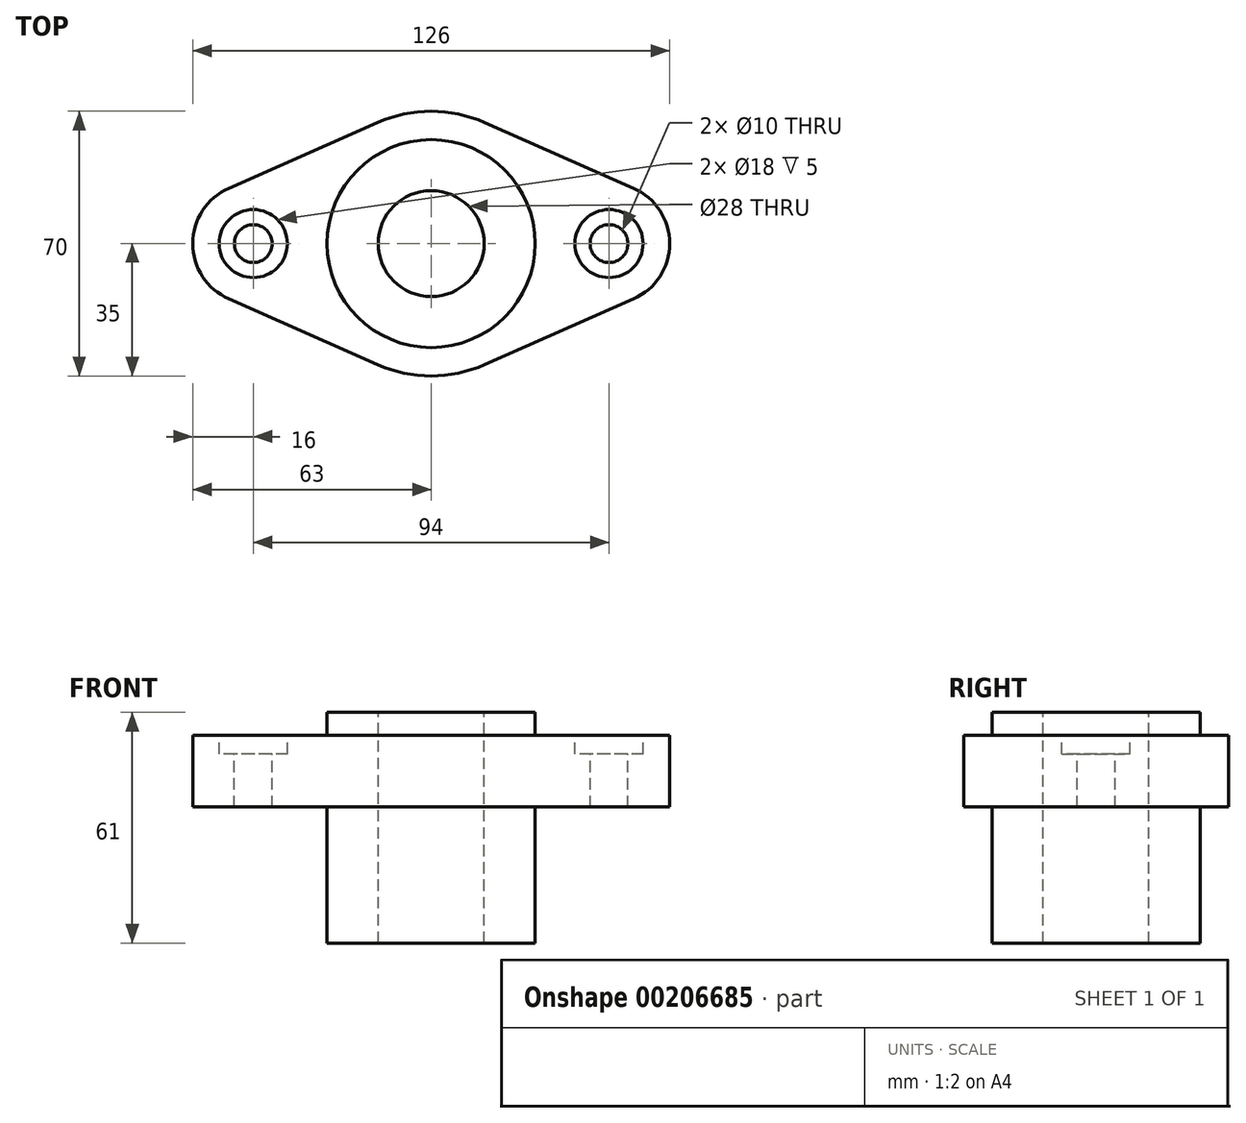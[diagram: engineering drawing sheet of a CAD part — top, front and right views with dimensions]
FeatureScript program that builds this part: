
annotation { "Feature Type Name" : "Feature", "Feature Type Description" : "" }
export const myFeature = defineFeature(function(context is Context, id is Id, definition is map)
    precondition{}
    {
        {
            var Q0;
            Q0=qCreatedBy(makeId("Top.planeOp"),FACE);
            var sketch = newSketch(context, id + "F0", { "sketchPlane" : qUnion([Q0])});
            skCircle(sketch, "E0", {"center": v(0, 0) * mm, "radius": 14 * mm});
            skCircle(sketch, "E1", {"center": v(0, 0) * mm, "radius": 27.5 * mm});
            skCircle(sketch, "E2", {"center": v(0, 0) * mm, "radius": 35 * mm});
            skCircle(sketch, "E3", {"center": v(-47, 0) * mm, "radius": 16 * mm});
            skCircle(sketch, "E4", {"center": v(47, 0) * mm, "radius": 16 * mm});
            skLineSegment(sketch, "E5", {"start": v(-53.47, 14.63) * mm, "end": v(-14.15, 32.01) * mm});
            skLineSegment(sketch, "E6", {"start": v(-53.47, -14.63) * mm, "end": v(-14.15, -32.01) * mm});
            skLineSegment(sketch, "E7", {"start": v(14.15, 32.01) * mm, "end": v(53.47, 14.63) * mm});
            skLineSegment(sketch, "E8", {"start": v(14.15, -32.01) * mm, "end": v(53.47, -14.63) * mm});
            skSolve(sketch);
        }
        {
            var Q0;
            {var subQ0=sQuery(id+"F0.wireOp",EDGE,"E3");var subQ1=sQuery(id+"F0.wireOp",EDGE,"E2");var subQ2=makeQuery(id+"F0.imprint","INTERSECT",VERTEX,{"disambiguationData":[OD(0.0)],"derivedFrom":[subQ1,subQ0]});Q0=makeQuery(id+"F0.imprint","IMPRINT",FACE,{"disambiguationData":[TD([[makeQuery(id+"F0.imprint","IMPRINT",EDGE,{"disambiguationData":[TD([[subQ2,-1.0]])],"derivedFrom":subQ1}),-1.0]])]});}
            var Q1;
            {var subQ0=sQuery(id+"F0.wireOp",EDGE,"E5");Q1=makeQuery(id+"F0.imprint","IMPRINT",FACE,{"disambiguationData":[TD([[makeQuery(id+"F0.imprint","IMPRINT",EDGE,{"derivedFrom":subQ0}),-1.0]])]});}
            var Q2;
            {var subQ0=sQuery(id+"F0.wireOp",EDGE,"E3");var subQ1=sQuery(id+"F0.wireOp",EDGE,"E2");var subQ2=makeQuery(id+"F0.imprint","INTERSECT",VERTEX,{"disambiguationData":[OD(0.0)],"derivedFrom":[subQ1,subQ0]});Q2=makeQuery(id+"F0.imprint","IMPRINT",FACE,{"disambiguationData":[TD([[makeQuery(id+"F0.imprint","IMPRINT",EDGE,{"disambiguationData":[TD([[subQ2,-1.0]])],"derivedFrom":subQ1}),1.0]])]});}
            var Q3;
            Q3=makeQuery(id+"F0.imprint","IMPRINT",FACE,{"disambiguationData":[TD([[makeQuery(id+"F0.imprint","IMPRINT",EDGE,{"derivedFrom":sQuery(id+"F0.wireOp",EDGE,"E1")}),-1.0]])]});
            var Q4;
            {var subQ0=sQuery(id+"F0.wireOp",EDGE,"E6");Q4=makeQuery(id+"F0.imprint","IMPRINT",FACE,{"disambiguationData":[TD([[makeQuery(id+"F0.imprint","IMPRINT",EDGE,{"derivedFrom":subQ0}),1.0]])]});}
            var Q5;
            Q5=makeQuery(id+"F0.imprint","IMPRINT",FACE,{"disambiguationData":[TD([[makeQuery(id+"F0.imprint","IMPRINT",EDGE,{"derivedFrom":sQuery(id+"F0.wireOp",EDGE,"E0")}),-1.0]])]});
            var Q6;
            {var subQ0=sQuery(id+"F0.wireOp",EDGE,"E4");var subQ1=sQuery(id+"F0.wireOp",EDGE,"E2");var subQ2=makeQuery(id+"F0.imprint","INTERSECT",VERTEX,{"disambiguationData":[OD(0.0)],"derivedFrom":[subQ1,subQ0]});Q6=makeQuery(id+"F0.imprint","IMPRINT",FACE,{"disambiguationData":[TD([[makeQuery(id+"F0.imprint","IMPRINT",EDGE,{"disambiguationData":[TD([[subQ2,1.0]])],"derivedFrom":subQ1}),-1.0]])]});}
            var Q7;
            {var subQ0=sQuery(id+"F0.wireOp",EDGE,"E4");var subQ1=sQuery(id+"F0.wireOp",EDGE,"E2");var subQ2=makeQuery(id+"F0.imprint","INTERSECT",VERTEX,{"disambiguationData":[OD(0.0)],"derivedFrom":[subQ1,subQ0]});Q7=makeQuery(id+"F0.imprint","IMPRINT",FACE,{"disambiguationData":[TD([[makeQuery(id+"F0.imprint","IMPRINT",EDGE,{"disambiguationData":[TD([[subQ2,1.0]])],"derivedFrom":subQ1}),1.0]])]});}
            var Q8;
            {var subQ0=sQuery(id+"F0.wireOp",EDGE,"E7");Q8=makeQuery(id+"F0.imprint","IMPRINT",FACE,{"disambiguationData":[TD([[makeQuery(id+"F0.imprint","IMPRINT",EDGE,{"derivedFrom":subQ0}),-1.0]])]});}
            var Q9;
            {var subQ0=sQuery(id+"F0.wireOp",EDGE,"E8");Q9=makeQuery(id+"F0.imprint","IMPRINT",FACE,{"disambiguationData":[TD([[makeQuery(id+"F0.imprint","IMPRINT",EDGE,{"derivedFrom":subQ0}),1.0]])]});}
            extrude(context, id + "F1", {"entities" : qUnion([Q0, Q1, Q2, Q3, Q4, Q5, Q6, Q7, Q8, Q9]), "oppositeDirection" : true, "depth" : 19 * mm});
        }
        {
            var Q0;
            Q0=makeQuery(id+"F0.imprint","IMPRINT",FACE,{"disambiguationData":[TD([[makeQuery(id+"F0.imprint","IMPRINT",EDGE,{"derivedFrom":sQuery(id+"F0.wireOp",EDGE,"E0")}),-1.0]])]});
            extrude(context, id + "F2", {"entities" : qUnion([Q0]), "operationType" : NewBodyOperationType.ADD, "depth" : 6 * mm});
        }
        {
            var Q0;
            Q0=makeQuery(id+"F1.opExtrude","CAP_FACE",FACE,{"disambiguationData":[OSD([sQuery(id+"F0.wireOp",EDGE,"E0"),sQuery(id+"F0.wireOp",EDGE,"E2"),sQuery(id+"F0.wireOp",EDGE,"E3"),sQuery(id+"F0.wireOp",EDGE,"E4"),sQuery(id+"F0.wireOp",EDGE,"E5"),sQuery(id+"F0.wireOp",EDGE,"E6"),sQuery(id+"F0.wireOp",EDGE,"E7"),sQuery(id+"F0.wireOp",EDGE,"E8")])],"isStart":false});
            var sketch = newSketch(context, id + "F3", { "sketchPlane" : qUnion([Q0])});
            skCircle(sketch, "E9", {"center": v(0, 0) * mm, "radius": 27.5 * mm});
            skCircle(sketch, "E10", {"center": v(0, 0) * mm, "radius": 14 * mm});
            skSolve(sketch);
        }
        {
            var Q0;
            Q0=makeQuery(id+"F3.imprint","IMPRINT",FACE,{"disambiguationData":[TD([[makeQuery(id+"F3.imprint","IMPRINT",EDGE,{"derivedFrom":sQuery(id+"F3.wireOp",EDGE,"E9")}),1.0]])]});
            extrude(context, id + "F4", {"entities" : qUnion([Q0]), "operationType" : NewBodyOperationType.ADD, "depth" : 36 * mm});
        }
        {
            var Q0;
            {var subQ0=sQuery(id+"F0.wireOp",EDGE,"E3");var subQ1=sQuery(id+"F0.wireOp",EDGE,"E2");var subQ2=makeQuery(id+"F0.imprint","INTERSECT",VERTEX,{"disambiguationData":[OD(0.0)],"derivedFrom":[subQ1,subQ0]});Q0=makeQuery(id+"F0.imprint","IMPRINT",FACE,{"disambiguationData":[TD([[makeQuery(id+"F0.imprint","IMPRINT",EDGE,{"disambiguationData":[TD([[subQ2,-1.0]])],"derivedFrom":subQ1}),-1.0]])]});}
            var sketch = newSketch(context, id + "F5", { "sketchPlane" : qUnion([Q0])});
            skPoint(sketch, "E11.0", {"position": v(47, 0) * mm});
            skPoint(sketch, "E12.0", {"position": v(-47, 0) * mm});
            skCircle(sketch, "E13", {"center": v(-47, 0) * mm, "radius": 5 * mm});
            skCircle(sketch, "E14", {"center": v(47, 0) * mm, "radius": 5 * mm});
            skSolve(sketch);
        }
        {
            var Q0;
            Q0 = qSketchRegion(id + "F5", true);
            extrude(context, id + "F6", {"entities" : qUnion([Q0]), "operationType" : NewBodyOperationType.REMOVE, "oppositeDirection" : true, "depth" : 25 * mm});
        }
        {
            var Q0;
            {var subQ0=sQuery(id+"F0.wireOp",EDGE,"E4");var subQ1=sQuery(id+"F0.wireOp",EDGE,"E2");var subQ2=makeQuery(id+"F0.imprint","INTERSECT",VERTEX,{"disambiguationData":[OD(0.0)],"derivedFrom":[subQ1,subQ0]});Q0=makeQuery(id+"F0.imprint","IMPRINT",FACE,{"disambiguationData":[TD([[makeQuery(id+"F0.imprint","IMPRINT",EDGE,{"disambiguationData":[TD([[subQ2,1.0]])],"derivedFrom":subQ1}),-1.0]])]});}
            var sketch = newSketch(context, id + "F7", { "sketchPlane" : qUnion([Q0])});
            skPoint(sketch, "E15.0", {"position": v(-47, 0) * mm});
            skPoint(sketch, "E16.0", {"position": v(47, 0) * mm});
            skCircle(sketch, "E17", {"center": v(-47, 0) * mm, "radius": 9 * mm});
            skCircle(sketch, "E18", {"center": v(47, 0) * mm, "radius": 9 * mm});
            skSolve(sketch);
        }
        {
            var Q0;
            Q0 = qSketchRegion(id + "F7", true);
            extrude(context, id + "F8", {"entities" : qUnion([Q0]), "operationType" : NewBodyOperationType.REMOVE, "oppositeDirection" : true, "depth" : 5 * mm});
        }
    });
